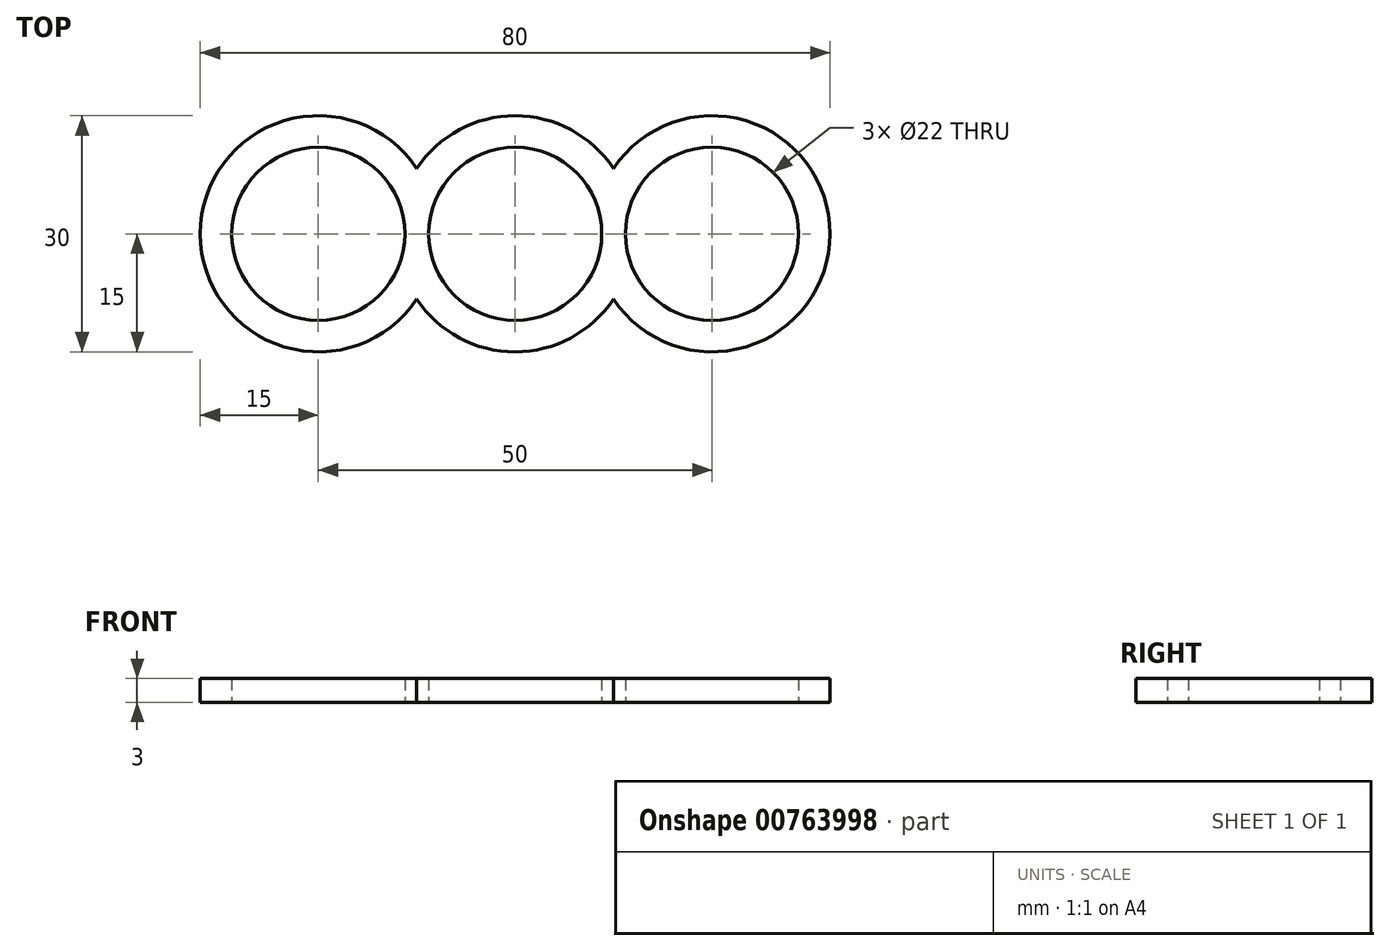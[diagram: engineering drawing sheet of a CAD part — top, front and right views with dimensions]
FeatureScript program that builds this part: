
annotation { "Feature Type Name" : "Feature", "Feature Type Description" : "" }
export const myFeature = defineFeature(function(context is Context, id is Id, definition is map)
    precondition{}
    {
        {
            var Q0;
            Q0=qCreatedBy(makeId("Top.planeOp"),FACE);
            var sketch = newSketch(context, id + "F0", { "sketchPlane" : qUnion([Q0])});
            skArc(sketch, "E0", {"start": v(0, 11) * mm, "mid": v(-11, 0) * mm, "end": v(0, -11) * mm});
            skArc(sketch, "E1", {"start": v(-12.5, -8.3) * mm, "mid": v(-7.1, -13.22) * mm, "end": v(0, -15) * mm});
            skLineSegment(sketch, "E2", {"start": v(-10, 0) * mm, "end": v(-11, 0) * mm});
            skCircle(sketch, "E3", {"center": v(-25, 0) * mm, "radius": 11 * mm});
            skArc(sketch, "E4", {"start": v(-12.5, 8.3) * mm, "mid": v(-40, 0) * mm, "end": v(-12.5, -8.3) * mm});
            skLineSegment(sketch, "E5.trimOffspring", {"start": v(-14, 0) * mm, "end": v(-15, 0) * mm});
            skLineSegment(sketch, "E6", {"start": v(-25, 0) * mm, "end": v(-25, -42.75) * mm});
            skArc(sketch, "E7.trimOffspring", {"start": v(0, 15) * mm, "mid": v(-7.1, 13.22) * mm, "end": v(-12.5, 8.3) * mm});
            skLineSegment(sketch, "E8.MirrorCS", {"start": v(10, 0) * mm, "end": v(11, 0) * mm});
            skLineSegment(sketch, "E9.MirrorCS", {"start": v(14, 0) * mm, "end": v(15, 0) * mm});
            skArc(sketch, "E10.MirrorCS", {"start": v(0, 11) * mm, "mid": v(11, 0) * mm, "end": v(0, -11) * mm});
            skArc(sketch, "E11.MirrorCS", {"start": v(12.5, -8.3) * mm, "mid": v(7.1, -13.22) * mm, "end": v(0, -15) * mm});
            skCircle(sketch, "E12.MirrorC", {"center": v(25, 0) * mm, "radius": 11 * mm});
            skArc(sketch, "E13.MirrorCS", {"start": v(12.5, 8.3) * mm, "mid": v(40, 0) * mm, "end": v(12.5, -8.3) * mm});
            skArc(sketch, "E14.MirrorCS", {"start": v(0, 15) * mm, "mid": v(7.1, 13.22) * mm, "end": v(12.5, 8.3) * mm});
            skSolve(sketch);
        }
        {
            var Q0;
            Q0 = qSketchRegion(id + "F0", true);
            extrude(context, id + "F1", {"entities" : qUnion([Q0]), "depth" : 3 * mm, "offsetDistance" : 25 * mm});
        }
    });
